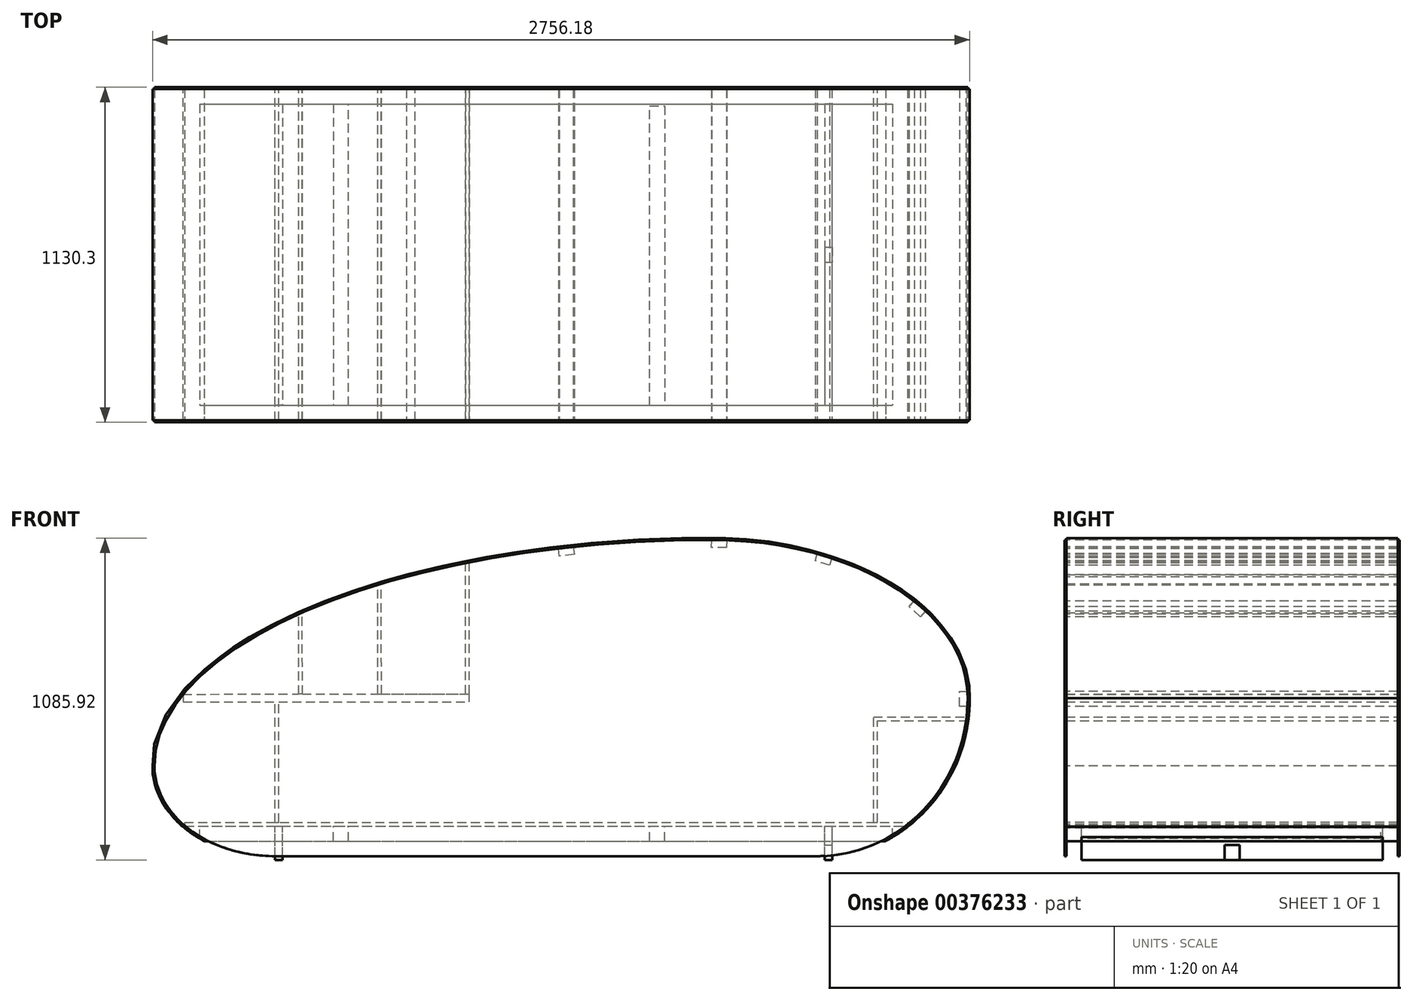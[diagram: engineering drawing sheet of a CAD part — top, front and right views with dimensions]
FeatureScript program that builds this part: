
annotation { "Feature Type Name" : "Feature", "Feature Type Description" : "" }
export const myFeature = defineFeature(function(context is Context, id is Id, definition is map)
    precondition{}
    {
        {
            var Q0;
            Q0=qCreatedBy(makeId("Top.planeOp"),FACE);
            var sketch = newSketch(context, id + "F0", { "sketchPlane" : qUnion([Q0])});
            skLineSegment(sketch, "E0.bottom", {"start": v(-1219.2, 558.8) * mm, "end": v(1219.2, 558.8) * mm});
            skLineSegment(sketch, "E0.top", {"start": v(-1219.2, -558.8) * mm, "end": v(1219.2, -558.8) * mm});
            skLineSegment(sketch, "E0.left", {"start": v(-1219.2, 558.8) * mm, "end": v(-1219.2, -558.8) * mm});
            skLineSegment(sketch, "E0.right", {"start": v(1219.2, 558.8) * mm, "end": v(1219.2, -558.8) * mm});
            skPoint(sketch, "E0.middle", {"position": v(0, 0) * mm});
            skSolve(sketch);
        }
        {
            var Q0;
            Q0 = qSketchRegion(id + "F0", true);
            extrude(context, id + "F1", {"entities" : qUnion([Q0]), "depth" : 12.7 * mm});
        }
        {
            var Q0;
            Q0=makeQuery(id+"F1.opExtrude","CAP_FACE",FACE,{"disambiguationData":[OSD([sQuery(id+"F0.wireOp",EDGE,"E0.bottom"),sQuery(id+"F0.wireOp",EDGE,"E0.top"),sQuery(id+"F0.wireOp",EDGE,"E0.left"),sQuery(id+"F0.wireOp",EDGE,"E0.right")])],"isStart":true});
            var sketch = newSketch(context, id + "F2", { "sketchPlane" : qUnion([Q0])});
            skLineSegment(sketch, "E1.bottom", {"start": v(-1219.2, 558.8) * mm, "end": v(1219.2, 558.8) * mm});
            skLineSegment(sketch, "E1.top", {"start": v(-1219.2, 508) * mm, "end": v(1219.2, 508) * mm});
            skLineSegment(sketch, "E1.left", {"start": v(-1219.2, 558.8) * mm, "end": v(-1219.2, 508) * mm});
            skLineSegment(sketch, "E1.right", {"start": v(1219.2, 558.8) * mm, "end": v(1219.2, 508) * mm});
            skLineSegment(sketch, "E2.bottom", {"start": v(-1219.2, -558.8) * mm, "end": v(1219.2, -558.8) * mm});
            skLineSegment(sketch, "E2.top", {"start": v(-1219.2, -508) * mm, "end": v(1219.2, -508) * mm});
            skLineSegment(sketch, "E2.left", {"start": v(-1219.2, -558.8) * mm, "end": v(-1219.2, -508) * mm});
            skLineSegment(sketch, "E2.right", {"start": v(1219.2, -558.8) * mm, "end": v(1219.2, -508) * mm});
            skLineSegment(sketch, "E3.bottom", {"start": v(-1219.2, 508) * mm, "end": v(-1168.4, 508) * mm});
            skLineSegment(sketch, "E3.top", {"start": v(-1219.2, -508) * mm, "end": v(-1168.4, -508) * mm});
            skLineSegment(sketch, "E3.left", {"start": v(-1219.2, 508) * mm, "end": v(-1219.2, -508) * mm});
            skLineSegment(sketch, "E3.right", {"start": v(-1168.4, 508) * mm, "end": v(-1168.4, -508) * mm});
            skLineSegment(sketch, "E4.bottom", {"start": v(1219.2, 508) * mm, "end": v(1168.4, 508) * mm});
            skLineSegment(sketch, "E4.top", {"start": v(1219.2, -508) * mm, "end": v(1168.4, -508) * mm});
            skLineSegment(sketch, "E4.left", {"start": v(1219.2, 508) * mm, "end": v(1219.2, -508) * mm});
            skLineSegment(sketch, "E4.right", {"start": v(1168.4, 508) * mm, "end": v(1168.4, -508) * mm});
            skSolve(sketch);
        }
        {
            var Q0;
            Q0 = qSketchRegion(id + "F2", true);
            var Q1;
            Q1=makeQuery(id+"F1.opExtrude","CAP_FACE",FACE,{"disambiguationData":[OSD([sQuery(id+"F0.wireOp",EDGE,"E0.bottom"),sQuery(id+"F0.wireOp",EDGE,"E0.top"),sQuery(id+"F0.wireOp",EDGE,"E0.left"),sQuery(id+"F0.wireOp",EDGE,"E0.right")])],"isStart":true});
            extrude(context, id + "F3", {"entities" : qUnion([Q0, Q1]), "depth" : 50.8 * mm});
        }
        {
            var Q0;
            Q0=makeQuery(id+"F0.imprint","IMPRINT",FACE,{"disambiguationData":[TD([[makeQuery(id+"F0.imprint","IMPRINT",EDGE,{"derivedFrom":sQuery(id+"F0.wireOp",EDGE,"E0.bottom")}),-1.0]])]});
            var sketch = newSketch(context, id + "F4", { "sketchPlane" : qUnion([Q0])});
            skPoint(sketch, "E5.middle", {"position": v(0, 0) * mm});
            skPoint(sketch, "E5.left.start.orphan", {"position": v(-1219.2, -609.6) * mm});
            skPoint(sketch, "E6.orphan", {"position": v(-1219.2, 609.6) * mm});
            skPoint(sketch, "E7.orphan", {"position": v(1219.2, -609.6) * mm});
            skPoint(sketch, "E8.orphan", {"position": v(1219.2, 609.6) * mm});
            skPoint(sketch, "E5.top.start.orphan", {"position": v(-1066.8, 609.6) * mm});
            skPoint(sketch, "E9.start.orphan", {"position": v(1041.4, -609.6) * mm});
            skLineSegment(sketch, "E10.top", {"start": v(-1066.8, 558.8) * mm, "end": v(-914.4, 558.8) * mm});
            skLineSegment(sketch, "E11", {"start": v(-914.4, 558.8) * mm, "end": v(-914.4, 508) * mm});
            skLineSegment(sketch, "E12", {"start": v(-914.4, 508) * mm, "end": v(-889, 508) * mm});
            skLineSegment(sketch, "E13", {"start": v(-889, 508) * mm, "end": v(-889, -508) * mm});
            skLineSegment(sketch, "E14", {"start": v(-889, -508) * mm, "end": v(-914.4, -508) * mm});
            skLineSegment(sketch, "E15", {"start": v(-914.4, -508) * mm, "end": v(-914.4, 508) * mm});
            skLineSegment(sketch, "E16.MirrorCS", {"start": v(914.4, 508) * mm, "end": v(889, 508) * mm});
            skLineSegment(sketch, "E17.MirrorCS", {"start": v(889, -508) * mm, "end": v(914.4, -508) * mm});
            skPoint(sketch, "E10.bottom.start.orphan", {"position": v(-1066.8, -558.8) * mm});
            skPoint(sketch, "E10.right.end.orphan", {"position": v(1066.8, 558.8) * mm});
            skPoint(sketch, "E10.right.start.orphan", {"position": v(1066.8, -558.8) * mm});
            skPoint(sketch, "E18.start.orphan", {"position": v(1066.8, 609.6) * mm});
            skLineSegment(sketch, "E19", {"start": v(939.8, -508) * mm, "end": v(965.2, -508) * mm});
            skLineSegment(sketch, "E20", {"start": v(965.2, -508) * mm, "end": v(965.2, 508) * mm});
            skLineSegment(sketch, "E21", {"start": v(965.2, 508) * mm, "end": v(939.8, 508) * mm});
            skLineSegment(sketch, "E22", {"start": v(939.8, 508) * mm, "end": v(939.8, -508) * mm});
            skPoint(sketch, "E23.MirrorCS.end.orphan", {"position": v(914.4, 508) * mm});
            skSolve(sketch);
        }
        {
            var Q0;
            Q0 = qSketchRegion(id + "F4", true);
            extrude(context, id + "F5", {"entities" : qUnion([Q0]), "oppositeDirection" : true, "depth" : 114.3 * mm});
        }
        {
            var Q0;
            Q0=makeQuery(id+"F3.opExtrude","SWEPT_FACE",FACE,{"disambiguationData":[OSD([sQuery(id+"F0.wireOp",EDGE,"E0.top")])]});
            cPlane(context, id + "F6", {"entities" : qUnion([Q0]), "cplaneType" : CPlaneType.OFFSET, "offset" : 0 * mm, "width" : 152.4 * mm, "height" : 152.4 * mm});
        }
        {
            var Q0;
            Q0=makeQuery(id+"F0.imprint","IMPRINT",FACE,{"disambiguationData":[TD([[makeQuery(id+"F0.imprint","IMPRINT",EDGE,{"derivedFrom":sQuery(id+"F0.wireOp",EDGE,"E0.bottom")}),-1.0]])]});
            var sketch = newSketch(context, id + "F7", { "sketchPlane" : qUnion([Q0])});
            skPoint(sketch, "E24.middle", {"position": v(0, 0) * mm});
            skLineSegment(sketch, "E25", {"start": v(-666.1, -508) * mm, "end": v(-666.1, 508) * mm});
            skLineSegment(sketch, "E26", {"start": v(-716.9, 508) * mm, "end": v(-716.9, -508) * mm});
            skLineSegment(sketch, "E27", {"start": v(349.9, -508) * mm, "end": v(349.9, 502.11) * mm});
            skLineSegment(sketch, "E28", {"start": v(400.7, 502.11) * mm, "end": v(400.7, -508) * mm});
            skPoint(sketch, "E29.start.orphan", {"position": v(-716.9, -609.6) * mm});
            skPoint(sketch, "E30.orphan", {"position": v(-1224.9, -609.6) * mm});
            skPoint(sketch, "E24.right.start.orphan", {"position": v(1224.9, -609.6) * mm});
            skPoint(sketch, "E24.top.end.orphan", {"position": v(1224.9, 609.6) * mm});
            skPoint(sketch, "E24.top.start.orphan", {"position": v(-1224.9, 609.6) * mm});
            skLineSegment(sketch, "E31", {"start": v(-716.9, 508) * mm, "end": v(-666.1, 508) * mm});
            skPoint(sketch, "E32.start.orphan", {"position": v(-716.9, 558.8) * mm});
            skLineSegment(sketch, "E33", {"start": v(-716.9, -508) * mm, "end": v(-666.1, -508) * mm});
            skLineSegment(sketch, "E34", {"start": v(349.9, -508) * mm, "end": v(400.7, -508) * mm});
            skPoint(sketch, "E35.orphan", {"position": v(400.7, -558.8) * mm});
            skPoint(sketch, "E36.start.orphan", {"position": v(349.9, -558.8) * mm});
            skLineSegment(sketch, "E37", {"start": v(349.9, 502.11) * mm, "end": v(400.7, 502.11) * mm});
            skSolve(sketch);
        }
        {
            var Q0;
            Q0 = qSketchRegion(id + "F7", true);
            extrude(context, id + "F8", {"entities" : qUnion([Q0]), "oppositeDirection" : true, "depth" : 50.8 * mm});
        }
        {
            var Q0;
            Q0=qCreatedBy(id+"F6.planeOp",FACE);
            var sketch = newSketch(context, id + "F9", { "sketchPlane" : qUnion([Q0])});
            skLineSegment(sketch, "E38", {"start": v(0, 0) * mm, "end": v(0, -101.6) * mm});
            skLineSegment(sketch, "E39", {"start": v(0, -101.6) * mm, "end": v(914.4, -101.6) * mm});
            skLineSegment(sketch, "E40", {"start": v(914.4, -101.6) * mm, "end": v(-914.4, -101.6) * mm});
            skLineSegment(sketch, "E41", {"start": v(-914.4, -101.6) * mm, "end": v(-914.4, 203.2) * mm});
            skLineSegment(sketch, "E42", {"start": v(-914.4, 203.2) * mm, "end": v(-1320.8, 203.2) * mm});
            skEllipticalArc(sketch, "E43", {});
            skLineSegment(sketch, "E44", {"start": v(-1320.8, 203.2) * mm, "end": v(558.8, 203.2) * mm});
            skLineSegment(sketch, "E45", {"start": v(558.8, 203.2) * mm, "end": v(558.8, 965.2) * mm});
            skEllipticalArc(sketch, "E46", {});
            skLineSegment(sketch, "E47", {"start": v(558.8, 203.2) * mm, "end": v(558.8, 431.8) * mm});
            skLineSegment(sketch, "E48", {"start": v(558.8, 431.8) * mm, "end": v(1422.4, 431.8) * mm});
            skEllipticalArc(sketch, "E49", {});
            skLineSegment(sketch, "E50", {"start": v(914.4, -101.6) * mm, "end": v(914.4, 431.8) * mm});
            skEllipticalArc(sketch, "E51", {});
            skLineSegment(sketch, "E52", {"start": v(-1219.29, 1.67) * mm, "end": v(-1219.29, -52.57) * mm});
            skLineSegment(sketch, "E53", {"start": v(-1219.29, -52.57) * mm, "end": v(-1135.45, -52.57) * mm});
            skLineSegment(sketch, "E54", {"start": v(1129.89, -51.23) * mm, "end": v(1220.38, -51.23) * mm});
            skLineSegment(sketch, "E55", {"start": v(1220.38, -51.23) * mm, "end": v(1220.38, 6) * mm});
            skFitSpline(sketch, "E56.0", {"points": [v(-1327.15, 203.2) * mm, v(-1327.15, 192.82) * mm, v(-1325.77, 172.15) * mm, v(-1319.7, 141.7) * mm, v(-1309.74, 112) * mm, v(-1296.03, 83.3) * mm, v(-1281.57, 60.35) * mm, v(-1268.25, 42.69) * mm, v(-1257.4, 29.81) * mm, v(-1245.71, 17.33) * mm, v(-1235.27, 7.28) * mm, v(-1226.52, -0.54) * mm, v(-1219.75, -6.28) * mm, v(-1213.94, -10.98) * mm, v(-1209.2, -14.67) * mm, v(-1205.59, -17.41) * mm, v(-1201.93, -20.12) * mm, v(-1197, -23.68) * mm, v(-1190.76, -28.03) * mm, v(-1183.1, -33.1) * mm, v(-1172.7, -39.65) * mm, v(-1159.36, -47.45) * mm, v(-1142.8, -56.18) * mm, v(-1125.73, -64.26) * mm, v(-1102.36, -74.18) * mm, v(-1072.05, -84.92) * mm, v(-1034.2, -95.08) * mm, v(-995.15, -102.45) * mm, v(-955.15, -106.93) * mm, v(-928.03, -107.95) * mm, v(-914.4, -107.95) * mm]});
            skFitSpline(sketch, "E56.1", {"points": [v(558.8, 971.55) * mm, v(496.85, 971.55) * mm, v(373.37, 969.07) * mm, v(190.65, 958.05) * mm, v(41.54, 942.9) * mm, v(-75.2, 927.28) * mm, v(-146.97, 916.07) * mm, v(-203.6, 906.24) * mm, v(-245.64, 898.43) * mm, v(-287.26, 890.2) * mm, v(-328.4, 881.56) * mm, v(-362.3, 874) * mm, v(-389.17, 867.73) * mm, v(-409.17, 862.94) * mm, v(-429, 858.05) * mm, v(-455.23, 851.4) * mm, v(-500.55, 839.45) * mm, v(-563.6, 821.44) * mm, v(-636.44, 798.38) * mm, v(-706.35, 773.92) * mm, v(-773.2, 748.12) * mm, v(-836.86, 721) * mm, v(-897.25, 692.64) * mm, v(-954.22, 663.06) * mm, v(-998.77, 637.44) * mm, v(-1032.58, 616.38) * mm, v(-1052.95, 602.99) * mm, v(-1068.77, 592.14) * mm, v(-1084.27, 581.2) * mm, v(-1103, 567.4) * mm, v(-1124.45, 550.63) * mm, v(-1151.67, 528) * mm, v(-1195.63, 487.76) * mm, v(-1247.88, 428.52) * mm, v(-1293.28, 355.1) * mm, v(-1320.91, 279.81) * mm, v(-1327.15, 228.8) * mm, v(-1327.15, 203.2) * mm]});
            skFitSpline(sketch, "E56.2", {"points": [v(1428.75, 431.8) * mm, v(1428.75, 449.7) * mm, v(1425.89, 485.36) * mm, v(1413.19, 538.1) * mm, v(1392.27, 589.65) * mm, v(1368.16, 631.31) * mm, v(1347.85, 659.63) * mm, v(1335.28, 675.55) * mm, v(1325.37, 687.35) * mm, v(1316.72, 697.06) * mm, v(1309.55, 704.76) * mm, v(1302.24, 712.4) * mm, v(1292.84, 721.83) * mm, v(1277.21, 736.65) * mm, v(1256.64, 754.69) * mm, v(1230.32, 775.5) * mm, v(1202.44, 795.46) * mm, v(1173.04, 814.53) * mm, v(1142.18, 832.67) * mm, v(1109.92, 849.87) * mm, v(1076.3, 866.08) * mm, v(1047.21, 878.75) * mm, v(1023.32, 888.35) * mm, v(1008.13, 894.13) * mm, v(995.84, 898.62) * mm, v(983.44, 903.02) * mm, v(967.8, 908.33) * mm, v(948.83, 914.41) * mm, v(923.24, 922.12) * mm, v(877.77, 934.56) * mm, v(810.97, 949.3) * mm, v(728.5, 962.07) * mm, v(644.27, 969.8) * mm, v(587.35, 971.55) * mm, v(558.8, 971.55) * mm]});
            skFitSpline(sketch, "E56.3", {"points": [v(914.4, -107.95) * mm, v(931.46, -107.95) * mm, v(965.41, -106.17) * mm, v(1015.47, -98.31) * mm, v(1064.33, -85.4) * mm, v(1111.65, -67.61) * mm, v(1149.51, -48.82) * mm, v(1178.7, -31.5) * mm, v(1199.99, -17.37) * mm, v(1220.64, -2.13) * mm, v(1237.28, 11.48) * mm, v(1250.24, 22.9) * mm, v(1259.76, 31.74) * mm, v(1267.55, 39.33) * mm, v(1273.67, 45.53) * mm, v(1278.22, 50.24) * mm, v(1282.7, 55.01) * mm, v(1288.6, 61.45) * mm, v(1295.83, 69.61) * mm, v(1304.25, 79.62) * mm, v(1315.12, 93.21) * mm, v(1328.08, 110.68) * mm, v(1342.59, 132.35) * mm, v(1356.03, 154.7) * mm, v(1372.52, 185.3) * mm, v(1390.4, 225.02) * mm, v(1407.32, 274.64) * mm, v(1419.59, 325.86) * mm, v(1427.06, 378.33) * mm, v(1428.75, 413.92) * mm, v(1428.75, 431.8) * mm]});
            const initialGuessF9  = {"E43": [-0.9144, 0.2032, -1, 0, 0.4064, 0.3048, 0, 1.5707963267948966], "E46": [0.5588, 0.2032, -1, 0, 1.8796, 0.762, 4.71238898038469, 0], "E49": [0.5588, 0.4318, 1, 0, 0.8636, 0.5334, 0, 1.5707963267948966], "E51": [0.9144, 0.4318, 0, -1, 0.5334, 0.508, 0, 1.5707963267948966]};
            skSetInitialGuess(sketch, initialGuessF9);
            skSolve(sketch);
        }
        {
            var Q0;
            Q0=makeQuery(id+"F9.imprint","IMPRINT",FACE,{"disambiguationData":[TD([[makeQuery(id+"F9.imprint","IMPRINT",EDGE,{"derivedFrom":sQuery(id+"F9.wireOp",EDGE,"E45")}),1.0]])]});
            var Q1;
            {var subQ0=sQuery(id+"F9.wireOp",EDGE,"E45");Q1=makeQuery(id+"F9.imprint","IMPRINT",FACE,{"disambiguationData":[TD([[makeQuery(id+"F9.imprint","IMPRINT",EDGE,{"derivedFrom":subQ0}),-1.0]])]});}
            var Q2;
            {var subQ1=sQuery(id+"F9.wireOp",EDGE,"E41");Q2=makeQuery(id+"F9.imprint","IMPRINT",FACE,{"disambiguationData":[TD([[makeQuery(id+"F9.imprint","IMPRINT",EDGE,{"derivedFrom":subQ1}),-1.0]])]});}
            var Q3;
            {var subQ3=sQuery(id+"F9.wireOp",EDGE,"E50");Q3=makeQuery(id+"F9.imprint","IMPRINT",FACE,{"disambiguationData":[TD([[makeQuery(id+"F9.imprint","IMPRINT",EDGE,{"derivedFrom":subQ3}),-1.0]])]});}
            var Q4;
            {var subQ1=sQuery(id+"F9.wireOp",EDGE,"E41");Q4=makeQuery(id+"F9.imprint","IMPRINT",FACE,{"disambiguationData":[TD([[makeQuery(id+"F9.imprint","IMPRINT",EDGE,{"derivedFrom":subQ1}),1.0]])]});}
            extrude(context, id + "F10", {"entities" : qUnion([Q0, Q1, Q2, Q3, Q4]), "depth" : 6.35 * mm});
        }
        {
            var Q0;
            Q0=makeQuery(id+"F10.opExtrude","SWEPT_BODY",BODY,{"disambiguationData":[OSD([sQuery(id+"F9.wireOp",EDGE,"E40"),sQuery(id+"F9.wireOp",EDGE,"E43"),sQuery(id+"F9.wireOp",EDGE,"E46"),sQuery(id+"F9.wireOp",EDGE,"E49"),sQuery(id+"F9.wireOp",EDGE,"E51")])]});
            var Q1;
            Q1=qCreatedBy(makeId("Front.planeOp"),FACE);
            mirror(context, id + "F11", {"entities" : qUnion([Q0]), "mirrorPlane" : qUnion([Q1])});
        }
        {
            var Q0;
            Q0=makeQuery(id+"F11.opPattern","COPY",FACE,{"derivedFrom":makeQuery(id+"F10.opExtrude","CAP_FACE",FACE,{"disambiguationData":[OSD([sQuery(id+"F9.wireOp",EDGE,"E40"),sQuery(id+"F9.wireOp",EDGE,"E43"),sQuery(id+"F9.wireOp",EDGE,"E46"),sQuery(id+"F9.wireOp",EDGE,"E49"),sQuery(id+"F9.wireOp",EDGE,"E51")])],"isStart":true}),"instanceName":"1"});
            var sketch = newSketch(context, id + "F12", { "sketchPlane" : qUnion([Q0])});
            skLineSegment(sketch, "E57", {"start": v(-914.4, -101.6) * mm, "end": v(-914.4, 12.7) * mm});
            skLineSegment(sketch, "E58", {"start": v(-914.4, 12.7) * mm, "end": v(-901.7, 12.7) * mm});
            skLineSegment(sketch, "E59", {"start": v(-901.7, 12.7) * mm, "end": v(-901.7, 419.1) * mm});
            skLineSegment(sketch, "E60", {"start": v(-1224.07, 444.5) * mm, "end": v(-1224.07, 419.1) * mm});
            skLineSegment(sketch, "E61", {"start": v(-914.4, 419.1) * mm, "end": v(-901.7, 419.1) * mm});
            skLineSegment(sketch, "E62", {"start": v(-914.4, 12.7) * mm, "end": v(-914.4, 419.1) * mm});
            skLineSegment(sketch, "E63", {"start": v(1117.4, 12.7) * mm, "end": v(1117.4, 355.6) * mm});
            skLineSegment(sketch, "E64", {"start": v(1117.4, 355.6) * mm, "end": v(1417.19, 355.6) * mm});
            skLineSegment(sketch, "E65.0", {"start": v(1104.7, 368.3) * mm, "end": v(1417.19, 368.3) * mm});
            skLineSegment(sketch, "E65.1", {"start": v(1104.7, 12.7) * mm, "end": v(1104.7, 368.3) * mm});
            skLineSegment(sketch, "E66", {"start": v(-1224.07, 444.5) * mm, "end": v(-555.18, 445.36) * mm});
            skLineSegment(sketch, "E67", {"start": v(-1224.07, 419.1) * mm, "end": v(-258.87, 419.1) * mm});
            skLineSegment(sketch, "E68", {"start": v(-258.87, 419.1) * mm, "end": v(-258.87, 445.74) * mm});
            skLineSegment(sketch, "E69", {"start": v(1104.7, 12.7) * mm, "end": v(1117.4, 12.7) * mm});
            skPoint(sketch, "E70.end.orphan", {"position": v(1104.7, 0) * mm});
            skLineSegment(sketch, "E71", {"start": v(1417.19, 355.6) * mm, "end": v(1417.19, 368.3) * mm});
            skLineSegment(sketch, "E72", {"start": v(-1224.07, 444.5) * mm, "end": v(-834.58, 445) * mm});
            skLineSegment(sketch, "E73", {"start": v(-834.58, 445) * mm, "end": v(-834.58, 714.57) * mm});
            skPoint(sketch, "E74.end.orphan", {"position": v(-603.8, 444.94) * mm});
            skEllipticalArc(sketch, "E75.trimOffspring", {});
            skLineSegment(sketch, "E76", {"start": v(-441.54, 848.27) * mm, "end": v(-441.54, 848.27) * mm});
            skLineSegment(sketch, "E77", {"start": v(-271.1, 445.73) * mm, "end": v(-271.66, 886.75) * mm});
            skLineSegment(sketch, "E78", {"start": v(-271.1, 445.73) * mm, "end": v(-258.4, 445.74) * mm});
            skEllipticalArc(sketch, "E79.trimOffspring", {});
            skEllipticalArc(sketch, "E80.trimOffspring", {});
            skEllipticalArc(sketch, "E81.trimOffspring", {});
            skPoint(sketch, "E82.center.orphan", {"position": v(558.8, 203.2) * mm});
            skEllipticalArc(sketch, "E83", {});
            skEllipticalArc(sketch, "E84.trimOffspring", {});
            skLineSegment(sketch, "E85", {"start": v(-603.8, 444.94) * mm, "end": v(-834.58, 445) * mm});
            skLineSegment(sketch, "E86", {"start": v(-258.87, 445.74) * mm, "end": v(-259.16, 889.22) * mm});
            skEllipticalArc(sketch, "E87.trimOffspring", {});
            skLineSegment(sketch, "E88", {"start": v(-834.58, 445) * mm, "end": v(-821.88, 445) * mm});
            skLineSegment(sketch, "E89", {"start": v(-821.88, 445) * mm, "end": v(-822.23, 720.04) * mm});
            skEllipticalArc(sketch, "E90", {});
            skEllipticalArc(sketch, "E91.trimOffspring", {});
            skEllipticalArc(sketch, "E92.trimOffspring", {});
            skEllipticalArc(sketch, "E93.trimOffspring", {});
            skEllipticalArc(sketch, "E94.trimOffspring", {});
            skEllipticalArc(sketch, "E95.trimOffspring", {});
            skEllipticalArc(sketch, "E96.trimOffspring", {});
            skEllipticalArc(sketch, "E97.trimOffspring", {});
            skLineSegment(sketch, "E98", {"start": v(-1224.07, 444.5) * mm, "end": v(-1224.07, 444.5) * mm});
            skLineSegment(sketch, "E99", {"start": v(-821.88, 445) * mm, "end": v(-567.88, 445.35) * mm});
            skLineSegment(sketch, "E100", {"start": v(-567.88, 445.35) * mm, "end": v(-567.88, 813.13) * mm});
            skLineSegment(sketch, "E101", {"start": v(-567.88, 445.35) * mm, "end": v(-555.18, 445.36) * mm});
            skLineSegment(sketch, "E102", {"start": v(-555.18, 445.36) * mm, "end": v(-555.66, 816.8) * mm});
            skLineSegment(sketch, "E103", {"start": v(-555.66, 816.8) * mm, "end": v(-567.88, 813.13) * mm});
            skLineSegment(sketch, "E104.trimOffspring", {"start": v(-271.1, 445.73) * mm, "end": v(-258.87, 445.74) * mm});
            skLineSegment(sketch, "E105", {"start": v(-555.18, 445.36) * mm, "end": v(-271.1, 445.73) * mm});
            const initialGuessF12  = {"E75.trimOffspring": [0.5577367636377379, 0.20377736741093452, -0.9999999527681334, -0.0003073495258862579, 1.8785368523645394, 0.7614121665525566, 5.162147941280892, 5.16954833158755], "E79.trimOffspring": [0.5577367636377379, 0.20377736741093452, -0.9999999527681334, -0.0003073495258862579, 1.8785368523645394, 0.7614121665525566, 5.273158447656821, 5.291712751635157], "E80.trimOffspring": [0.5577367636442481, 0.20377736740824748, -0.9999999527681338, -0.0003073495246283011, 1.8785368523713388, 0.761412166555361, 5.162147941283503, 5.169548331590141], "E81.trimOffspring": [0.5577367636442481, 0.2037773674082475, -0.9999999527681338, -0.0003073495246283011, 1.8785368523713388, 0.761412166555361, 5.537337606657416, 5.547074962675175], "E83": [0.5577367636377379, 0.20377736741093455, -0.9999995162097849, -0.0009836565439138747, 1.8808462317359835, 0.7617069904081163, 5.161281476949313, 5.168670628661571], "E84.trimOffspring": [0.5577367636425947, 0.2037773674089412, -0.9999999527681337, -0.00030734952495059975, 1.8785368523696089, 0.7614121665546388, 5.162147941282839, 5.169548331589483], "E87.trimOffspring": [0.6925762697527742, 0.2406099761735075, -1, 0, 1.8796, 0.762, 5.360123035606801, 5.360161641424304], "E90": [0.5577367636377379, 0.20377736741093452, -0.9999999527681335, -0.0003073495258863059, 1.8785368523645398, 0.7614121665525564, 5.162147941280892, 5.16954833158755], "E91.trimOffspring": [0.5577367636377379, 0.20377736741093452, -0.9999999527681335, -0.0003073495258863059, 1.8785368523645398, 0.7614121665525564, 5.537337606655717, 5.547074962673499], "E92.trimOffspring": [0.55886707639725, 0.20316164772175863, -1, 0, 1.879599998871934, 0.7620061310171642, 5.273637886068248, 5.292185878433573], "E93.trimOffspring": [0.5577367636377379, 0.20377736741093452, -0.9999999527681334, -0.0003073495258862579, 1.8785368523645394, 0.7614121665525566, 5.537337606655718, 5.547074962673499], "E81.trimOffspring": [0.5577367636442481, 0.2037773674082475, -0.9999999527681338, -0.0003073495246283011, 1.8785368523713388, 0.761412166555361, 5.537337606657416, 5.5470749626751745], "E94.trimOffspring": [0.5577367636442481, 0.2037773674082475, -0.9999999527681338, -0.0003073495246283011, 1.8785368523713388, 0.761412166555361, 5.162147941283503, 5.169548331590141], "E75.trimOffspring": [0.5577367636377379, 0.20377736741093452, -0.9999999527681334, -0.0003073495258862579, 1.8785368523645394, 0.7614121665525566, 5.162147941280892, 5.16954833158755], "E95.trimOffspring": [0.5577367636425947, 0.20377736740894123, -0.9999999527681338, -0.00030734952495059986, 1.8785368523696089, 0.7614121665546388, 5.273158447658559, 5.291712751640683], "E96.trimOffspring": [0.5577367636377379, 0.20377736741093455, -0.9999995162097849, -0.0009836565439138747, 1.8808462317359835, 0.7617069904081163, 5.272113770693625, 5.290635939511727], "E97.trimOffspring": [0.5577367636442481, 0.2037773674082475, -0.9999999527681338, -0.0003073495246283011, 1.8785368523713388, 0.761412166555361, 5.273158447659149, 5.29171275163744], "E94.trimOffspring": [0.5577367636442481, 0.2037773674082475, -0.9999999527681338, -0.0003073495246283011, 1.8785368523713388, 0.761412166555361, 5.162147941283504, 5.169548331590141]};
            skSetInitialGuess(sketch, initialGuessF12);
            skSolve(sketch);
        }
        {
            var Q0;
            {var subQ3=sQuery(id+"F12.wireOp",EDGE,"E60");Q0=makeQuery(id+"F12.imprint","IMPRINT",FACE,{"disambiguationData":[TD([[makeQuery(id+"F12.imprint","IMPRINT",EDGE,{"derivedFrom":subQ3}),1.0]])]});}
            var Q1;
            Q1=makeQuery(id+"F12.imprint","IMPRINT",FACE,{"disambiguationData":[TD([[makeQuery(id+"F12.imprint","IMPRINT",EDGE,{"derivedFrom":sQuery(id+"F12.wireOp",EDGE,"E58")}),1.0]])]});
            extrude(context, id + "F13", {"entities" : qUnion([Q0, Q1]), "depth" : 1117.6 * mm});
        }
        {
            var Q0;
            Q0=makeQuery(id+"F12.imprint","IMPRINT",FACE,{"disambiguationData":[TD([[makeQuery(id+"F12.imprint","IMPRINT",EDGE,{"derivedFrom":sQuery(id+"F12.wireOp",EDGE,"E63")}),1.0]])]});
            extrude(context, id + "F14", {"entities" : qUnion([Q0]), "depth" : 1117.6 * mm});
        }
        {
            var Q0;
            {var subQ0=sQuery(id+"F9.wireOp",EDGE,"E54");Q0=makeQuery(id+"F9.imprint","IMPRINT",FACE,{"disambiguationData":[TD([[makeQuery(id+"F9.imprint","IMPRINT",EDGE,{"derivedFrom":subQ0}),1.0]])]});}
            var Q1;
            {var subQ0=sQuery(id+"F9.wireOp",EDGE,"E52");Q1=makeQuery(id+"F9.imprint","IMPRINT",FACE,{"disambiguationData":[TD([[makeQuery(id+"F9.imprint","IMPRINT",EDGE,{"derivedFrom":subQ0}),1.0]])]});}
            extrude(context, id + "F15", {"entities" : qUnion([Q0, Q1]), "operationType" : NewBodyOperationType.REMOVE, "endBound" : BoundingType.THROUGH_ALL, "oppositeDirection" : true, "depth" : 1117.6 * mm});
        }
        {
            var Q0;
            Q0 = qSketchRegion(id + "F12", true);
            extrude(context, id + "F16", {"entities" : qUnion([Q0]), "depth" : 1117.6 * mm});
        }
        {
            var Q0;
            {var subQ0=sQuery(id+"F9.wireOp",EDGE,"E45");Q0=makeQuery(id+"F9.imprint","IMPRINT",FACE,{"disambiguationData":[TD([[makeQuery(id+"F9.imprint","IMPRINT",EDGE,{"derivedFrom":subQ0}),-1.0]])]});}
            var sketch = newSketch(context, id + "F17", { "sketchPlane" : qUnion([Q0])});
            skEllipticalArc(sketch, "E106", {});
            skLineSegment(sketch, "E107", {"start": v(41.8, 935.8) * mm, "end": v(92.3, 941.36) * mm});
            skLineSegment(sketch, "E108", {"start": v(92.3, 941.36) * mm, "end": v(95.08, 916.11) * mm});
            skLineSegment(sketch, "E109", {"start": v(95.08, 916.11) * mm, "end": v(44.58, 910.56) * mm});
            skLineSegment(sketch, "E110", {"start": v(44.58, 910.56) * mm, "end": v(41.8, 935.8) * mm});
            skLineSegment(sketch, "E111", {"start": v(1395, 431.8) * mm, "end": v(1422.4, 431.8) * mm});
            skEllipticalArc(sketch, "E112.trimOffspring", {});
            skLineSegment(sketch, "E113", {"start": v(558.8, 965.2) * mm, "end": v(609.59, 964.13) * mm});
            skLineSegment(sketch, "E114", {"start": v(609.59, 964.13) * mm, "end": v(609.05, 938.73) * mm});
            skLineSegment(sketch, "E115", {"start": v(609.05, 938.73) * mm, "end": v(558.26, 939.8) * mm});
            skLineSegment(sketch, "E116", {"start": v(558.26, 939.8) * mm, "end": v(558.8, 965.2) * mm});
            skLineSegment(sketch, "E117", {"start": v(915.19, 918.93) * mm, "end": v(963.88, 904.45) * mm});
            skLineSegment(sketch, "E118", {"start": v(963.88, 904.45) * mm, "end": v(956.64, 880.1) * mm});
            skLineSegment(sketch, "E119", {"start": v(956.64, 880.1) * mm, "end": v(907.95, 894.58) * mm});
            skLineSegment(sketch, "E120", {"start": v(907.95, 894.58) * mm, "end": v(915.19, 918.93) * mm});
            skLineSegment(sketch, "E121", {"start": v(1241.85, 758.68) * mm, "end": v(1279.75, 724.85) * mm});
            skLineSegment(sketch, "E122", {"start": v(1279.75, 724.85) * mm, "end": v(1262.83, 705.9) * mm});
            skLineSegment(sketch, "E123", {"start": v(1262.83, 705.9) * mm, "end": v(1224.93, 739.73) * mm});
            skLineSegment(sketch, "E124", {"start": v(1224.93, 739.73) * mm, "end": v(1241.85, 758.68) * mm});
            skLineSegment(sketch, "E125", {"start": v(1420.4, 454.44) * mm, "end": v(1420.4, 403.64) * mm});
            skLineSegment(sketch, "E126", {"start": v(1420.4, 403.64) * mm, "end": v(1395, 403.64) * mm});
            skLineSegment(sketch, "E127", {"start": v(1395, 403.64) * mm, "end": v(1395, 454.44) * mm});
            skLineSegment(sketch, "E128", {"start": v(1395, 454.44) * mm, "end": v(1420.4, 454.44) * mm});
            skEllipticalArc(sketch, "E129.trimOffspring", {});
            skEllipticalArc(sketch, "E130.trimOffspring", {});
            skEllipticalArc(sketch, "E131.trimOffspring", {});
            skLineSegment(sketch, "E132.trimOffspring", {"start": v(558.8, 939.8) * mm, "end": v(558.8, 965.2) * mm});
            skPoint(sketch, "E133.end.orphan", {"position": v(-1320.8, 203.2) * mm});
            const initialGuessF17  = {"E106": [0.5588, 0.2032, -1, 0, 1.8796, 0.762, 4.963199327868331, 4.991035164101439], "E112.trimOffspring": [0.38798218375571075, 0.30242656633685144, 0.9864308829351479, 0.16417707876492607, 1.0438314444917323, 0.6490599817194953, 6.218107263660173, 6.253068905848729], "E129.trimOffspring": [0.38798218375571075, 0.30242656633685144, 0.9864308829351479, 0.16417707876492607, 1.0438314444917323, 0.6490599817194953, 1.2519250700460411, 1.3019000048510254], "E130.trimOffspring": [0.38798218375571075, 0.30242656633685144, 0.9864308829351479, 0.16417707876492607, 1.0438314444917323, 0.6490599817194953, 0.8777062190264827, 0.9333087124605587], "E131.trimOffspring": [0.38798218375571075, 0.30242656633685144, 0.9864308829351479, 0.16417707876492607, 1.0438314444917323, 0.6490599817194953, 0.42951539609831774, 0.4977227023022919]};
            skSetInitialGuess(sketch, initialGuessF17);
            skSolve(sketch);
        }
        {
            var Q0;
            Q0 = qSketchRegion(id + "F17", true);
            extrude(context, id + "F18", {"entities" : qUnion([Q0]), "oppositeDirection" : true, "depth" : 1117.6 * mm});
        }
        {
            var Q0;
            {var subQ5=sQuery(id+"F9.wireOp",EDGE,"E46");Q0=makeQuery(id+"F9.imprint","IMPRINT",FACE,{"disambiguationData":[TD([[makeQuery(id+"F9.imprint","IMPRINT",EDGE,{"derivedFrom":subQ5}),-1.0]])]});}
            extrude(context, id + "F19", {"entities" : qUnion([Q0]), "oppositeDirection" : true, "depth" : 1117.6 * mm});
        }
        {
            var Q0;
            Q0=makeQuery(id+"F5.opExtrude","SWEPT_FACE",FACE,{"disambiguationData":[OSD([sQuery(id+"F4.wireOp",EDGE,"E20")])]});
            var sketch = newSketch(context, id + "F20", { "sketchPlane" : qUnion([Q0])});
            skLineSegment(sketch, "E134", {"start": v(-25.4, -101.6) * mm, "end": v(-25.4, -63.5) * mm});
            skLineSegment(sketch, "E135", {"start": v(-25.4, -114.3) * mm, "end": v(-25.4, -63.5) * mm});
            skLineSegment(sketch, "E136", {"start": v(-25.4, -63.5) * mm, "end": v(0, -63.5) * mm});
            skPoint(sketch, "E137.orphan", {"position": v(0, -50.8) * mm});
            skPoint(sketch, "E138.start.orphan", {"position": v(0, -114.3) * mm});
            skLineSegment(sketch, "E139", {"start": v(-25.4, -114.3) * mm, "end": v(25.4, -114.3) * mm});
            skLineSegment(sketch, "E140", {"start": v(25.4, -114.3) * mm, "end": v(25.4, -63.5) * mm});
            skLineSegment(sketch, "E141", {"start": v(25.4, -63.5) * mm, "end": v(-25.4, -63.5) * mm});
            skSolve(sketch);
        }
        {
            var Q0;
            Q0 = qSketchRegion(id + "F20", true);
            extrude(context, id + "F21", {"entities" : qUnion([Q0]), "operationType" : NewBodyOperationType.REMOVE, "endBound" : BoundingType.UP_TO_NEXT, "oppositeDirection" : true, "depth" : 25.4 * mm});
        }
    });
